FCSTD DOCUMENT  (FreeCAD 0.20R0.20.2)
Label: 004
License: All rights reserved
LicenseURL: http://en.wikipedia.org/wiki/All_rights_reserved
objects: Sketcher::SketchObject×1
note: 1 computed .brp shape members not serialized (recipe doc carries the construction recipe); baked Part::Feature solids carry a one-line shape summary decoded from their .brp

FEATURE [Sketcher::SketchObject] Sketch
  FullyConstrained = true
  sketch-geometry (25):
    g0: Circle CenterX=7 CenterY=2e-16 CenterZ=0 NormalX=0 NormalY=0 NormalZ=1 AngleXU=0 Radius=2
    g1: Circle CenterX=0 CenterY=7 CenterZ=0 NormalX=0 NormalY=0 NormalZ=1 AngleXU=0 Radius=2
    g2: Circle CenterX=0 CenterY=0 CenterZ=0 NormalX=0 NormalY=0 NormalZ=1 AngleXU=0 Radius=2.8
    g3: Circle CenterX=-7 CenterY=1e-16 CenterZ=0 NormalX=0 NormalY=0 NormalZ=1 AngleXU=0 Radius=2
    g4: Circle CenterX=0 CenterY=-7 CenterZ=0 NormalX=0 NormalY=0 NormalZ=1 AngleXU=0 Radius=2
    g5: LineSegment StartX=18.75 StartY=10.5 StartZ=0 EndX=18.75 EndY=-10.5 EndZ=0
    g6: LineSegment StartX=-18.75 StartY=10.5 StartZ=0 EndX=-18.75 EndY=-10.5 EndZ=0
    g7: LineSegment StartX=-16.55 StartY=8.3 StartZ=0 EndX=-3.5 EndY=8.3 EndZ=0
    g8: LineSegment StartX=-3.5 StartY=8.3 StartZ=0 EndX=-3.5 EndY=3.5 EndZ=0
    g9: LineSegment StartX=-3.5 StartY=3.5 StartZ=0 EndX=-16.55 EndY=3.5 EndZ=0
    g10: LineSegment StartX=-16.55 StartY=3.5 StartZ=0 EndX=-16.55 EndY=8.3 EndZ=0
    g11: LineSegment StartX=16.55 StartY=8.3 StartZ=0 EndX=3.5 EndY=8.3 EndZ=0
    g12: LineSegment StartX=3.5 StartY=8.3 StartZ=0 EndX=3.5 EndY=3.5 EndZ=0
    g13: LineSegment StartX=3.5 StartY=3.5 StartZ=0 EndX=16.55 EndY=3.5 EndZ=0
    g14: LineSegment StartX=16.55 StartY=3.5 StartZ=0 EndX=16.55 EndY=8.3 EndZ=0
    g15: LineSegment StartX=-16.55 StartY=-8.3 StartZ=0 EndX=-3.5 EndY=-8.3 EndZ=0
    g16: LineSegment StartX=-3.5 StartY=-8.3 StartZ=0 EndX=-3.5 EndY=-3.5 EndZ=0
    g17: LineSegment StartX=-3.5 StartY=-3.5 StartZ=0 EndX=-16.55 EndY=-3.5 EndZ=0
    g18: LineSegment StartX=-16.55 StartY=-3.5 StartZ=0 EndX=-16.55 EndY=-8.3 EndZ=0
    g19: LineSegment StartX=16.55 StartY=-8.3 StartZ=0 EndX=3.5 EndY=-8.3 EndZ=0
    g20: LineSegment StartX=3.5 StartY=-8.3 StartZ=0 EndX=3.5 EndY=-3.5 EndZ=0
    g21: LineSegment StartX=3.5 StartY=-3.5 StartZ=0 EndX=16.55 EndY=-3.5 EndZ=0
    g22: LineSegment StartX=16.55 StartY=-3.5 StartZ=0 EndX=16.55 EndY=-8.3 EndZ=0
    g23: LineSegment StartX=-18.75 StartY=10.5 StartZ=0 EndX=18.75 EndY=10.5 EndZ=0
    g24: LineSegment StartX=18.75 StartY=-10.5 StartZ=0 EndX=-18.75 EndY=-10.5 EndZ=0
  constraints (67):
    c: Block(g2)
    c: Block(g1)
    c: Block(g0)
    c: Block(g3)
    c: Block(g4)
    c: Vertical(g5)
    c: Vertical(g6)
    c: Coincident(g7,g8)
    c: Coincident(g8,g9)
    c: Coincident(g9,g10)
    c: Coincident(g10,g7)
    c: Horizontal(g7)
    c: Horizontal(g9)
    c: Vertical(g8)
    c: Vertical(g10)
    c: Block(g6)
    c: Distance(g6) = 21
    c: Distance(g5) = 21
    c: Coincident(g11,g12)
    c: Coincident(g12,g13)
    c: Coincident(g13,g14)
    c: Coincident(g14,g11)
    c: Horizontal(g11)
    c: Horizontal(g13)
    c: Vertical(g12)
    c: Vertical(g14)
    c: Block(g11)
    c: Block(g7)
    c: Block(g8)
    c: Block(g9)
    c: Block(g10)
    c: Block(g13)
    c: Block(g12)
    c: Block(g14)
    c: Coincident(g15,g16)
    c: Coincident(g16,g17)
    c: Coincident(g17,g18)
    c: Coincident(g18,g15)
    c: Horizontal(g15)
    c: Horizontal(g17)
    c: Vertical(g16)
    c: Vertical(g18)
    c: Coincident(g19,g20)
    c: Coincident(g20,g21)
    c: Coincident(g21,g22)
    c: Coincident(g22,g19)
    c: Horizontal(g19)
    c: Horizontal(g21)
    c: Vertical(g20)
    c: Vertical(g22)
    c: Block(g21)
    c: Block(g22)
    c: Block(g19)
    c: Block(g20)
    c: Block(g16)
    c: Block(g15)
    c: Block(g17)
    c: Block(g18)
    c: Block(g5)
    c: Coincident(g23,g6)
    c: Coincident(g23,g5)
    c: Horizontal(g23)
    c: Coincident(g24,g5)
    c: Coincident(g24,g6)
    c: Horizontal(g24)
    c: Block(g23)
    c: Block(g24)
